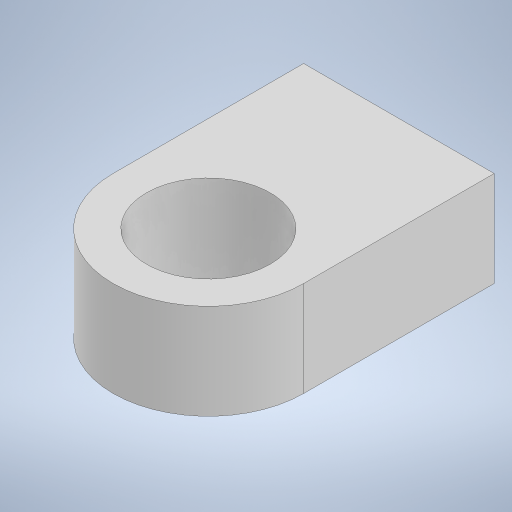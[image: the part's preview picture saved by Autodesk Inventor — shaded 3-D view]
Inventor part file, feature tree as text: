
AUTODESK INVENTOR PART (.ipt)
format: ipt  version: 2023 (Build 270158000, 158)  size: 200,192 bytes
history: native  units: mm
features: extrude x1, sketch x1
ambient origin geometry x8: Origin, YZ Plane, XZ Plane, XY Plane, X Axis, Y Axis, Z Axis, Center Point
bodies: Solido1 (feature_tree)
feature tree (2):
  extrude  "Estrusione1"  Depth=13.0mm
  sketch  "Schizzo2"
